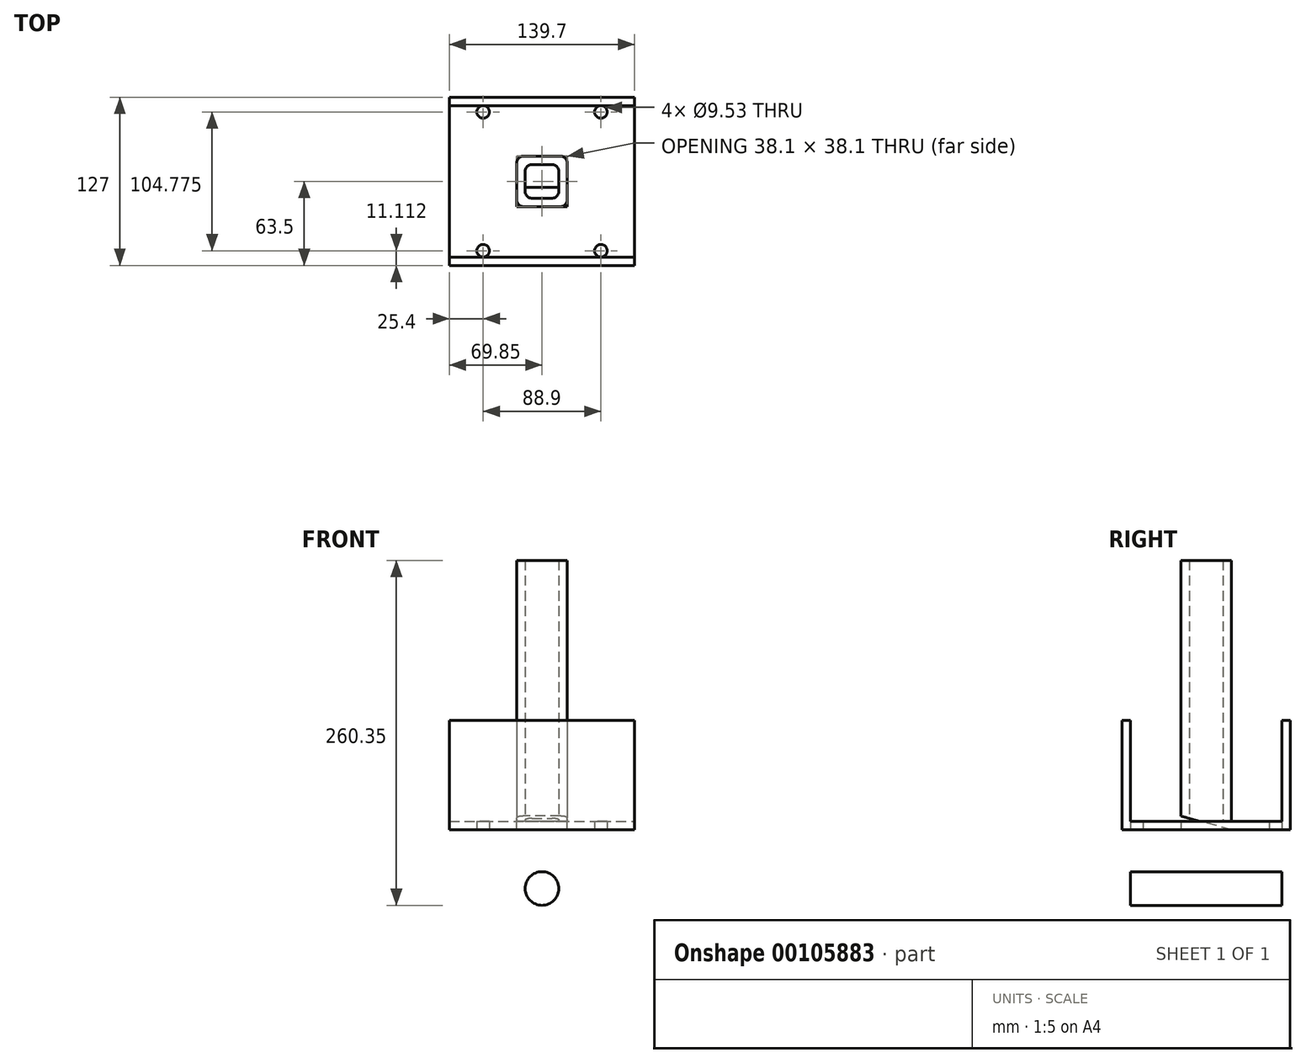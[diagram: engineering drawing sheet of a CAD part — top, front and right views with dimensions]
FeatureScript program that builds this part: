
annotation { "Feature Type Name" : "Feature", "Feature Type Description" : "" }
export const myFeature = defineFeature(function(context is Context, id is Id, definition is map)
    precondition{}
    {
        {
            var Q0;
            Q0=qCreatedBy(makeId("Top.planeOp"),FACE);
            var sketch = newSketch(context, id + "F0", { "sketchPlane" : qUnion([Q0])});
            skLineSegment(sketch, "E0.bottom", {"start": v(19.05, 19.05) * mm, "end": v(-19.05, 19.05) * mm});
            skLineSegment(sketch, "E0.top", {"start": v(19.05, -19.05) * mm, "end": v(-19.05, -19.05) * mm});
            skLineSegment(sketch, "E0.left", {"start": v(19.05, 19.05) * mm, "end": v(19.05, -19.05) * mm});
            skLineSegment(sketch, "E0.right", {"start": v(-19.05, 19.05) * mm, "end": v(-19.05, -19.05) * mm});
            skPoint(sketch, "E0.middle", {"position": v(0, 0) * mm});
            skLineSegment(sketch, "E1.0", {"start": v(12.7, 12.7) * mm, "end": v(-12.7, 12.7) * mm});
            skLineSegment(sketch, "E1.1", {"start": v(12.7, 12.7) * mm, "end": v(12.7, -12.7) * mm});
            skLineSegment(sketch, "E1.2", {"start": v(12.7, -12.7) * mm, "end": v(-12.7, -12.7) * mm});
            skLineSegment(sketch, "E1.3", {"start": v(-12.7, 12.7) * mm, "end": v(-12.7, -12.7) * mm});
            skSolve(sketch);
        }
        {
            var Q0;
            Q0=qSketchRegion(id+"F0",true);
            extrude(context, id + "F1", {"entities" : qUnion([Q0]), "depth" : 203.2 * mm});
        }
        {
            var Q0;
            Q0=makeQuery(id+"F1.opExtrude","SWEPT_EDGE",EDGE,{"disambiguationData":[OSD([sQuery(id+"F0.wireOp",EDGE,"E0.bottom"),sQuery(id+"F0.wireOp",EDGE,"E0.right")])]});
            var Q1;
            Q1=makeQuery(id+"F1.opExtrude","SWEPT_EDGE",EDGE,{"disambiguationData":[OSD([sQuery(id+"F0.wireOp",EDGE,"E0.top"),sQuery(id+"F0.wireOp",EDGE,"E0.right")])]});
            var Q2;
            Q2=makeQuery(id+"F1.opExtrude","SWEPT_EDGE",EDGE,{"disambiguationData":[OSD([sQuery(id+"F0.wireOp",EDGE,"E0.top"),sQuery(id+"F0.wireOp",EDGE,"E0.left")])]});
            var Q3;
            Q3=makeQuery(id+"F1.opExtrude","SWEPT_EDGE",EDGE,{"disambiguationData":[OSD([sQuery(id+"F0.wireOp",EDGE,"E0.bottom"),sQuery(id+"F0.wireOp",EDGE,"E0.left")])]});
            var Q4;
            Q4=makeQuery(id+"F1.opExtrude","SWEPT_EDGE",EDGE,{"disambiguationData":[OSD([sQuery(id+"F0.wireOp",EDGE,"E1.0"),sQuery(id+"F0.wireOp",EDGE,"E1.3")])]});
            var Q5;
            Q5=makeQuery(id+"F1.opExtrude","SWEPT_EDGE",EDGE,{"disambiguationData":[OSD([sQuery(id+"F0.wireOp",EDGE,"E1.0"),sQuery(id+"F0.wireOp",EDGE,"E1.1")])]});
            var Q6;
            Q6=makeQuery(id+"F1.opExtrude","SWEPT_EDGE",EDGE,{"disambiguationData":[OSD([sQuery(id+"F0.wireOp",EDGE,"E1.1"),sQuery(id+"F0.wireOp",EDGE,"E1.2")])]});
            var Q7;
            Q7=makeQuery(id+"F1.opExtrude","SWEPT_EDGE",EDGE,{"disambiguationData":[OSD([sQuery(id+"F0.wireOp",EDGE,"E1.2"),sQuery(id+"F0.wireOp",EDGE,"E1.3")])]});
            fillet(context, id + "F2", {"entities" : qUnion([Q0, Q1, Q2, Q3, Q4, Q5, Q6, Q7]), "radius" : 5.08 * mm, "tangentPropagation" : true, "allowEdgeOverflow" : false});
        }
        {
            var Q0;
            Q0=qCreatedBy(makeId("Top.planeOp"),FACE);
            var sketch = newSketch(context, id + "F3", { "sketchPlane" : qUnion([Q0])});
            skLineSegment(sketch, "E2.bottom", {"start": v(-69.85, -63.5) * mm, "end": v(69.85, -63.5) * mm});
            skLineSegment(sketch, "E2.top", {"start": v(-69.85, 63.5) * mm, "end": v(69.85, 63.5) * mm});
            skLineSegment(sketch, "E2.left", {"start": v(-69.85, -63.5) * mm, "end": v(-69.85, 63.5) * mm});
            skLineSegment(sketch, "E2.right", {"start": v(69.85, -63.5) * mm, "end": v(69.85, 63.5) * mm});
            skPoint(sketch, "E2.middle", {"position": v(0, 0) * mm});
            skCircle(sketch, "E3", {"center": v(-44.45, -52.39) * mm, "radius": 4.76 * mm});
            skLineSegment(sketch, "E4", {"start": v(69.85, -9.52) * mm, "end": v(-69.85, -9.53) * mm, "construction": true});
            skLineSegment(sketch, "E5.MirrorCS", {"start": v(69.85, 9.52) * mm, "end": v(-69.85, 9.53) * mm, "construction": true});
            skCircle(sketch, "E6.MirrorC", {"center": v(-44.45, 52.39) * mm, "radius": 4.76 * mm});
            skCircle(sketch, "E7.MirrorC", {"center": v(44.45, -52.39) * mm, "radius": 4.76 * mm});
            skCircle(sketch, "E8.MirrorC", {"center": v(44.45, 52.39) * mm, "radius": 4.76 * mm});
            skSolve(sketch);
        }
        {
            var Q0;
            Q0=qSketchRegion(id+"F3",true);
            extrude(context, id + "F4", {"entities" : qUnion([Q0]), "operationType" : NewBodyOperationType.ADD, "depth" : 6.35 * mm});
        }
        {
            var Q0;
            Q0=makeQuery(id+"F4.opExtrude","CAP_FACE",FACE,{"disambiguationData":[OSD([sQuery(id+"F3.wireOp",EDGE,"E2.bottom"),sQuery(id+"F3.wireOp",EDGE,"E2.top"),sQuery(id+"F3.wireOp",EDGE,"E2.left"),sQuery(id+"F3.wireOp",EDGE,"E2.right"),sQuery(id+"F3.wireOp",EDGE,"E3"),sQuery(id+"F3.wireOp",EDGE,"E6.MirrorC"),sQuery(id+"F3.wireOp",EDGE,"E7.MirrorC"),sQuery(id+"F3.wireOp",EDGE,"E8.MirrorC")])],"isStart":false});
            var sketch = newSketch(context, id + "F5", { "sketchPlane" : qUnion([Q0])});
            skLineSegment(sketch, "E9.bottom", {"start": v(-69.85, -63.5) * mm, "end": v(69.85, -63.5) * mm});
            skLineSegment(sketch, "E9.top", {"start": v(-69.85, 63.5) * mm, "end": v(69.85, 63.5) * mm});
            skLineSegment(sketch, "E9.left", {"start": v(-69.85, -63.5) * mm, "end": v(-69.85, 63.5) * mm});
            skLineSegment(sketch, "E9.right", {"start": v(69.85, -63.5) * mm, "end": v(69.85, 63.5) * mm});
            skPoint(sketch, "E9.middle", {"position": v(0, 0) * mm});
            skSolve(sketch);
        }
        {
            var Q0;
            Q0=makeQuery(id+"F5.imprint","IMPRINT",FACE,{"disambiguationData":[TD([[makeQuery(id+"F5.imprint","IMPRINT",EDGE,{"derivedFrom":sQuery(id+"F5.wireOp",EDGE,"E9.bottom")}),1.0]])]});
            var sketch = newSketch(context, id + "F6", { "sketchPlane" : qUnion([Q0])});
            skLineSegment(sketch, "E10.bottom", {"start": v(-69.85, 63.5) * mm, "end": v(69.85, 63.5) * mm});
            skLineSegment(sketch, "E10.top", {"start": v(-69.85, 57.15) * mm, "end": v(69.85, 57.15) * mm});
            skLineSegment(sketch, "E10.left", {"start": v(-69.85, 63.5) * mm, "end": v(-69.85, 57.15) * mm});
            skLineSegment(sketch, "E10.right", {"start": v(69.85, 63.5) * mm, "end": v(69.85, 57.15) * mm});
            skLineSegment(sketch, "E11.MirrorCS", {"start": v(-69.85, -57.15) * mm, "end": v(69.85, -57.15) * mm});
            skLineSegment(sketch, "E12.MirrorCS", {"start": v(69.85, -63.5) * mm, "end": v(69.85, -57.15) * mm});
            skLineSegment(sketch, "E13.MirrorCS", {"start": v(-69.85, -63.5) * mm, "end": v(69.85, -63.5) * mm});
            skLineSegment(sketch, "E14.MirrorCS", {"start": v(-69.85, -63.5) * mm, "end": v(-69.85, -57.15) * mm});
            skSolve(sketch);
        }
        {
            var Q0;
            Q0=qSketchRegion(id+"F6",true);
            extrude(context, id + "F7", {"entities" : qUnion([Q0]), "operationType" : NewBodyOperationType.ADD, "depth" : 76.2 * mm});
        }
        {
            var Q0;
            Q0=makeQuery(id+"F7.opExtrude","SWEPT_FACE",FACE,{"disambiguationData":[OSD([sQuery(id+"F6.wireOp",EDGE,"E10.top")])]});
            var sketch = newSketch(context, id + "F8", { "sketchPlane" : qUnion([Q0])});
            skCircle(sketch, "E15", {"center": v(0, -44.45) * mm, "radius": 12.7 * mm});
            skLineSegment(sketch, "E16", {"start": v(63.5, -44.45) * mm, "end": v(-63.5, -44.45) * mm, "construction": true});
            skLineSegment(sketch, "E17", {"start": v(0, -6.35) * mm, "end": v(0, -82.55) * mm, "construction": true});
            skSolve(sketch);
        }
        {
            var Q0;
            Q0=makeQuery(id+"F8.imprint","IMPRINT",FACE,{"disambiguationData":[TD([[makeQuery(id+"F8.imprint","IMPRINT",EDGE,{"derivedFrom":sQuery(id+"F8.wireOp",EDGE,"E15")}),1.0]])]});
            var Q1;
            Q1=sQuery(id+"F8.wireOp",EDGE,"E15");
            var Q2;
            Q2=makeQuery(id+"F7.opExtrude","SWEPT_FACE",FACE,{"disambiguationData":[OSD([sQuery(id+"F6.wireOp",EDGE,"E11.MirrorCS")])]});
            extrude(context, id + "F9", {"entities" : qUnion([Q0]), "operationType" : NewBodyOperationType.ADD, "surfaceEntities" : qUnion([Q1]), "endBound" : BoundingType.UP_TO_SURFACE, "endBoundEntityFace" : qUnion([Q2]), "depth" : 25.4 * mm});
        }
        {
            var Q0;
            {var subQ0=makeQuery(id+"F1.opExtrude","SWEPT_FACE",FACE,{"disambiguationData":[OSD([sQuery(id+"F0.wireOp",EDGE,"E0.right")])]});Q0=makeQuery(id+"Fp0Iko9FnHYjrbP_1.boolean.opBoolean","MERGE",FACE,{"derivedFrom":[subQ0,makeQuery(id+"Fp0Iko9FnHYjrbP_1.opPattern","COPY",FACE,{"derivedFrom":subQ0,"instanceName":"1"})]});}
            var sketch = newSketch(context, id + "F10", { "sketchPlane" : qUnion([Q0])});
            skLineSegment(sketch, "E18", {"start": v(-19.05, 0) * mm, "end": v(19.05, 10.2) * mm});
            skLineSegment(sketch, "E19", {"start": v(19.05, 10.2) * mm, "end": v(19.05, 0) * mm});
            skLineSegment(sketch, "E20", {"start": v(19.05, 0) * mm, "end": v(-19.05, 0) * mm});
            skSolve(sketch);
        }
        {
            var Q0;
            Q0=qSketchRegion(id+"F10",true);
            var Q1;
            {var subQ0=makeQuery(id+"F1.opExtrude","SWEPT_FACE",FACE,{"disambiguationData":[OSD([sQuery(id+"F0.wireOp",EDGE,"E0.left")])]});Q1=makeQuery(id+"Fp0Iko9FnHYjrbP_1.boolean.opBoolean","MERGE",FACE,{"derivedFrom":[subQ0,makeQuery(id+"Fp0Iko9FnHYjrbP_1.opPattern","COPY",FACE,{"derivedFrom":subQ0,"instanceName":"1"})]});}
            extrude(context, id + "F11", {"entities" : qUnion([Q0]), "operationType" : NewBodyOperationType.REMOVE, "endBound" : BoundingType.UP_TO_SURFACE, "oppositeDirection" : true, "endBoundEntityFace" : qUnion([Q1]), "depth" : 25.4 * mm});
        }
    });
